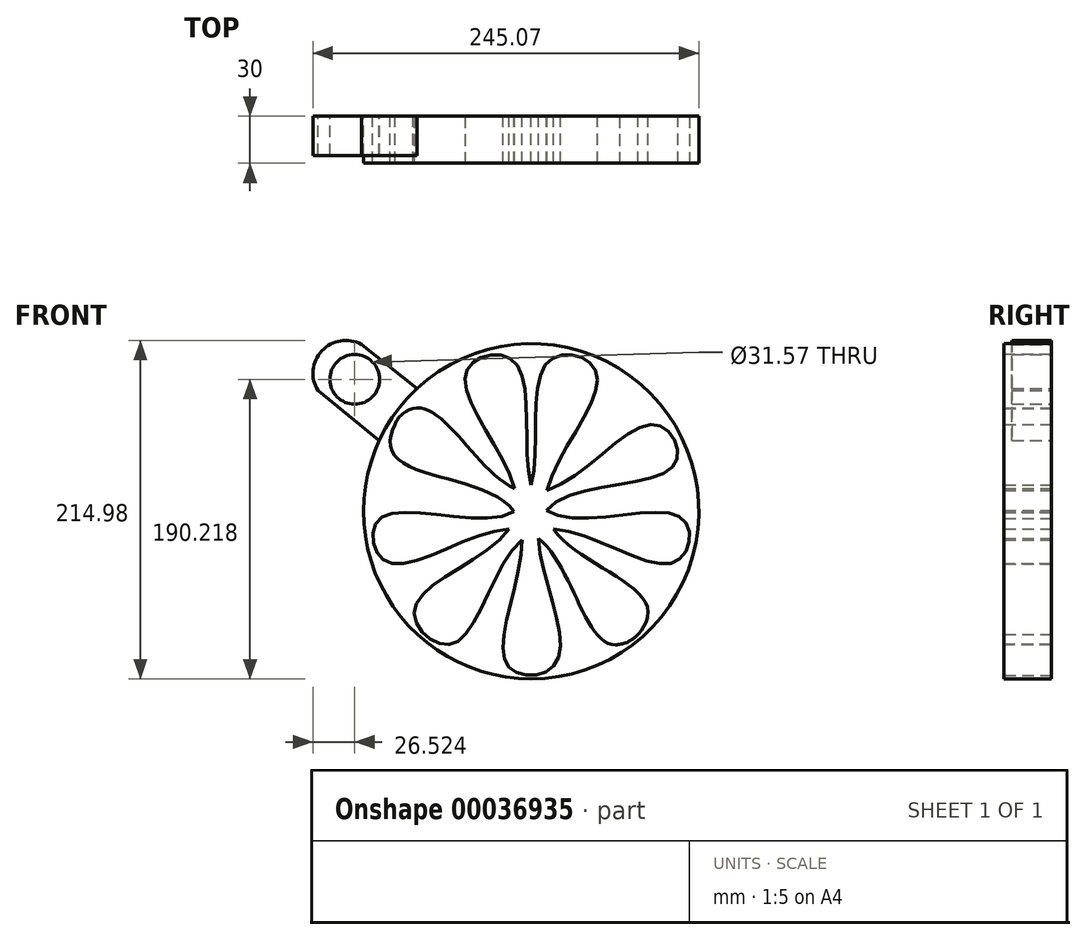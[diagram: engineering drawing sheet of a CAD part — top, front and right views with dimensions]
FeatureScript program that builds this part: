
annotation { "Feature Type Name" : "Feature", "Feature Type Description" : "" }
export const myFeature = defineFeature(function(context is Context, id is Id, definition is map)
    precondition{}
    {
        {
            var Q0;
            Q0=qCreatedBy(makeId("Front.planeOp"),FACE);
            var sketch = newSketch(context, id + "F0", { "sketchPlane" : qUnion([Q0])});
            skCircle(sketch, "E0", {"center": v(0, 8.44) * mm, "radius": 106.47 * mm});
            skPoint(sketch, "E1", {"position": v(2.27, -7.9) * mm});
            skPoint(sketch, "E2", {"position": v(100.16, -12.01) * mm});
            skPoint(sketch, "E3", {"position": v(-27.86, 107.39) * mm});
            skFitSpline(sketch, "E4", {"points": [v(-9.62, 6.36) * mm, v(-73.92, -52.87) * mm, v(-49.74, -75.75) * mm, v(2.27, -4.63) * mm, v(90.48, -24.17) * mm, v(95.33, 4.24) * mm, v(7.99, 10.35) * mm, v(-10.14, 102.74) * mm, v(-41.75, 95.66) * mm, v(-9.62, 6.36) * mm]});
            skFitSpline(sketch, "E5.MirrorCS", {"points": [v(9.62, 6.36) * mm, v(73.92, -52.87) * mm, v(49.74, -75.75) * mm, v(-2.27, -4.63) * mm, v(-90.48, -24.17) * mm, v(-95.33, 4.24) * mm, v(-7.99, 10.35) * mm, v(10.14, 102.74) * mm, v(41.75, 95.66) * mm, v(9.62, 6.36) * mm]});
            skPoint(sketch, "E6.MirrorP", {"position": v(-2.27, -7.9) * mm});
            skArc(sketch, "E7", {"start": v(53.69, -76.38) * mm, "mid": v(61.38, -74.6) * mm, "end": v(67.7, -69.86) * mm});
            skLineSegment(sketch, "E8", {"start": v(-72.65, 86.28) * mm, "end": v(-107.83, 114.43) * mm});
            skLineSegment(sketch, "E9", {"start": v(-96.47, 53.49) * mm, "end": v(-135.46, 85.1) * mm});
            skArc(sketch, "E10", {"start": v(-107.83, 114.43) * mm, "mid": v(-132.92, 110.4) * mm, "end": v(-135.46, 85.1) * mm});
            skCircle(sketch, "E11", {"center": v(-112.08, 92.19) * mm, "radius": 15.79 * mm});
            skLineSegment(sketch, "E12", {"start": v(-9.62, 6.36) * mm, "end": v(9.62, 9.08) * mm});
            skFitSpline(sketch, "E13.MirrorCS", {"points": [v(-9.62, 6.36) * mm, v(-87.82, 45.43) * mm, v(-70.95, 74.12) * mm, v(-1.25, 20.22) * mm, v(78.08, 63.46) * mm, v(90.63, 37.5) * mm, v(8.4, 7.4) * mm, v(16.62, -86.39) * mm, v(-15.71, -88.35) * mm, v(-9.62, 6.36) * mm]});
            skArc(sketch, "E14", {"start": v(-74.91, 73.63) * mm, "mid": v(-82.02, 70.03) * mm, "end": v(-86.56, 63.47) * mm});
            skSolve(sketch);
        }
        {
            var Q0;
            Q0=makeQuery(id+"F0.imprint","IMPRINT",FACE,{"disambiguationData":[TD([[makeQuery(id+"F0.imprint","IMPRINT",EDGE,{"derivedFrom":sQuery(id+"F0.wireOp",EDGE,"bc6ea9b0-a48d-4d8b-8419-accb068e8f06")}),-1.0]])]});
            var Q1;
            Q1=makeQuery(id+"F0.imprint","IMPRINT",FACE,{"disambiguationData":[TD([[makeQuery(id+"F0.imprint","IMPRINT",EDGE,{"derivedFrom":sQuery(id+"F0.wireOp",EDGE,"E0")}),1.0]])]});
            var Q2;
            {var subQ5=sQuery(id+"F0.wireOp",EDGE,"E4");Q2=makeQuery(id+"F0.imprint","IMPRINT",FACE,{"disambiguationData":[TD([[makeQuery(id+"F0.imprint","IMPRINT",EDGE,{"derivedFrom":subQ5}),-1.0]])]});}
            extrude(context, id + "F1", {"entities" : qUnion([Q0, Q1, Q2]), "depth" : 30 * mm});
        }
        {
            var Q0;
            {var subQ1=sQuery(id+"F0.wireOp",EDGE,"E8");Q0=makeQuery(id+"F0.imprint","IMPRINT",FACE,{"disambiguationData":[TD([[makeQuery(id+"F0.imprint","IMPRINT",EDGE,{"derivedFrom":subQ1}),1.0]])]});}
            extrude(context, id + "F2", {"entities" : qUnion([Q0]), "operationType" : NewBodyOperationType.ADD, "depth" : 25 * mm});
        }
    });
